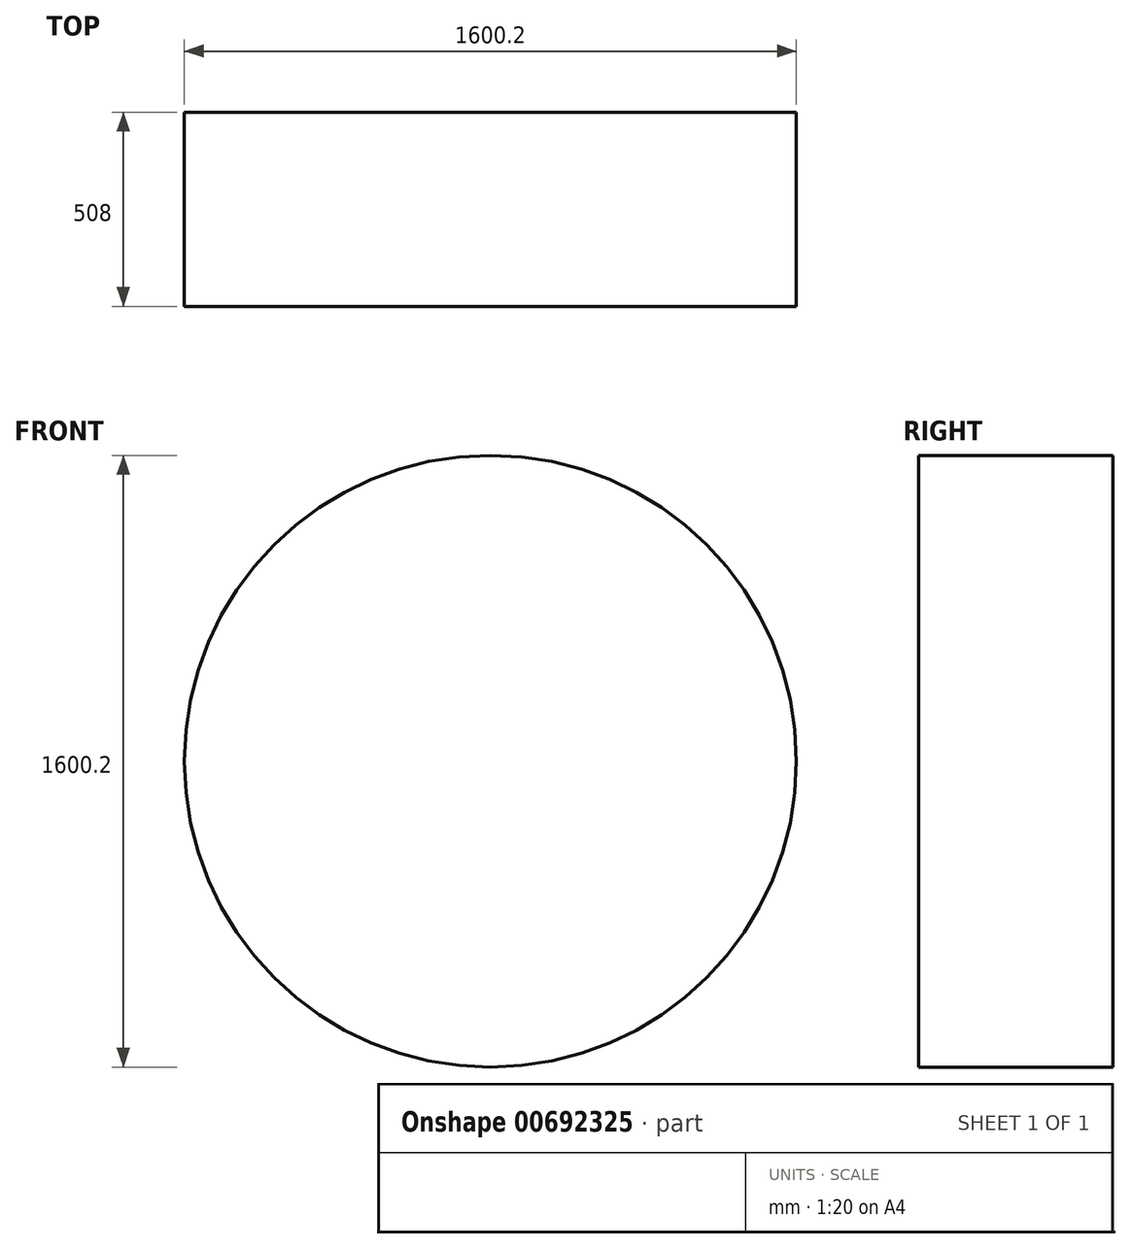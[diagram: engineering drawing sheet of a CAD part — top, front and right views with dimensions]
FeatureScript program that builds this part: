
annotation { "Feature Type Name" : "Feature", "Feature Type Description" : "" }
export const myFeature = defineFeature(function(context is Context, id is Id, definition is map)
    precondition{}
    {
        {
            var Q0;
            Q0=qCreatedBy(makeId("Front.planeOp"),FACE);
            var sketch = newSketch(context, id + "F0", { "sketchPlane" : qUnion([Q0])});
            skCircle(sketch, "E0", {"center": v(0, 0) * mm, "radius": 800.1 * mm});
            skSolve(sketch);
        }
        {
            var Q0;
            Q0 = qSketchRegion(id + "F0", true);
            extrude(context, id + "F1", {"entities" : qUnion([Q0]), "depth" : 508 * mm, "offsetDistance" : 25.4 * mm});
        }
    });
